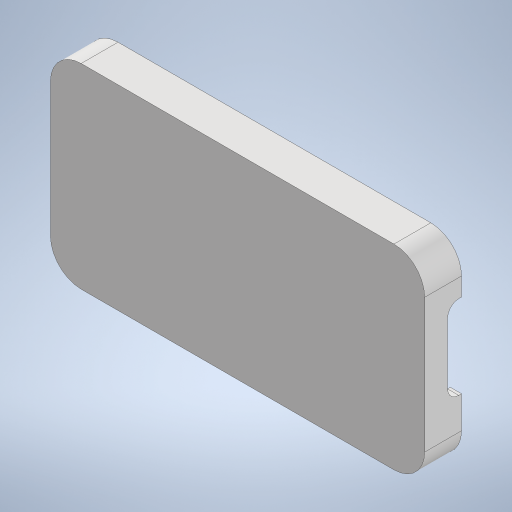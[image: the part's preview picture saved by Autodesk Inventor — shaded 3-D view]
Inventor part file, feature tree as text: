
AUTODESK INVENTOR PART (.ipt)
format: ipt  version: 2023 (Build 270158000, 158)  size: 310,784 bytes
history: native  units: in
note: dims shown in document units (in); Inventor stores cm internally (conversion verified against a paired STEP export)
features: reference x13, extrude x5, sketch x5, other x4, fillet x3, projected_geometry x2, plane x1
ambient origin geometry x8: Origin, YZ Plane, XZ Plane, XY Plane, X Axis, Y Axis, Z Axis, Center Point
bodies: Solid1 (feature_tree)
feature tree (33):
  extrude  "Extrusion1"  Depth=0.1102in
  extrude  "Extrusion2"  Depth=0.1181in
  fillet  "Fillet1"  Radius=0.1181in
  sketch  "Sketch3"  dims[d6=0.0787in d7=0.0in d8=0.1181in]
  plane  "Work Plane1"
  extrude  "Extrusion3"  Depth=0.1181in
  extrude  "Extrusion4"  Depth=0.2963in TaperAngle=0.0deg
  extrude  "Extrusion5"  Depth=0.3937in TaperAngle=0.0deg
  fillet  "Fillet2"  Radius=0.0984in
  fillet  "Fillet3"  Radius=0.8563in
  sketch  "Sketch1"  dims[d0=0.2362in d1=0.1102in]
  reference  "Reference1"
  reference  "Reference2"
  reference  "Reference3"
  reference  "Reference4"
  reference  "Reference5"
  reference  "Reference6"
  reference  "Reference7"
  sketch  "Sketch2"  dims[d2=0.1102in d3=0.1102in d4=0.1181in d5=0.0in]
  reference  "Reference8"
  reference  "Reference9"
  reference  "Reference10"
  reference  "Reference11"
  projected_geometry  "Projected Loop1"
  sketch  "Sketch4"  dims[d9=0.0984in d10=0.2963in d11=0.0in]
  projected_geometry  "Projected Loop2"
  sketch  "Sketch5"  dims[d12=0.0197in d13=0.3937in d14=0.0in d15=0.0984in d16=0.8563in d17=0.0in d18=0.0787in d19=0.0787in]
  reference  "Reference12"
  reference  "Reference13"
  other  "<userpath>\Nextcloud2\private\HAMpower\Case\case_assambly.iam"
  other  "case_assambly.iam"
  other  "powerplay:1"
  other  "Case_Cap:1"
